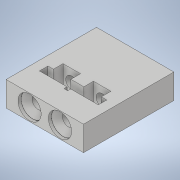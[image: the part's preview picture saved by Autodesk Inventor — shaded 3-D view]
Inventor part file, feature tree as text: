
AUTODESK INVENTOR PART (.ipt)
format: ipt  version: 2020 (Build 240168000, 168)  size: 174,080 bytes
history: native  units: mm
features: extrude x4, sketch x4, other x2, chamfer x1
ambient origin geometry x8: Origin, YZ Plane, XZ Plane, XY Plane, X Axis, Y Axis, Z Axis, Center Point
bodies: Solide1 (feature_tree)
feature tree (11):
  extrude  "Extrusion1"  Depth=75.0mm
  extrude  "Extrusion2"  Depth=19.5mm
  extrude  "Extrusion3"  Depth=2.8mm
  chamfer  "Chanfrein1"  Distance=8.0mm
  other  "Axe de construction1"
  other  "Axe de construction2"
  extrude  "Extrusion4"  Depth=8.2mm TaperAngle=0.0deg
  sketch  "Esquisse1"
  sketch  "Esquisse2"
  sketch  "Esquisse3"
  sketch  "Esquisse5"
